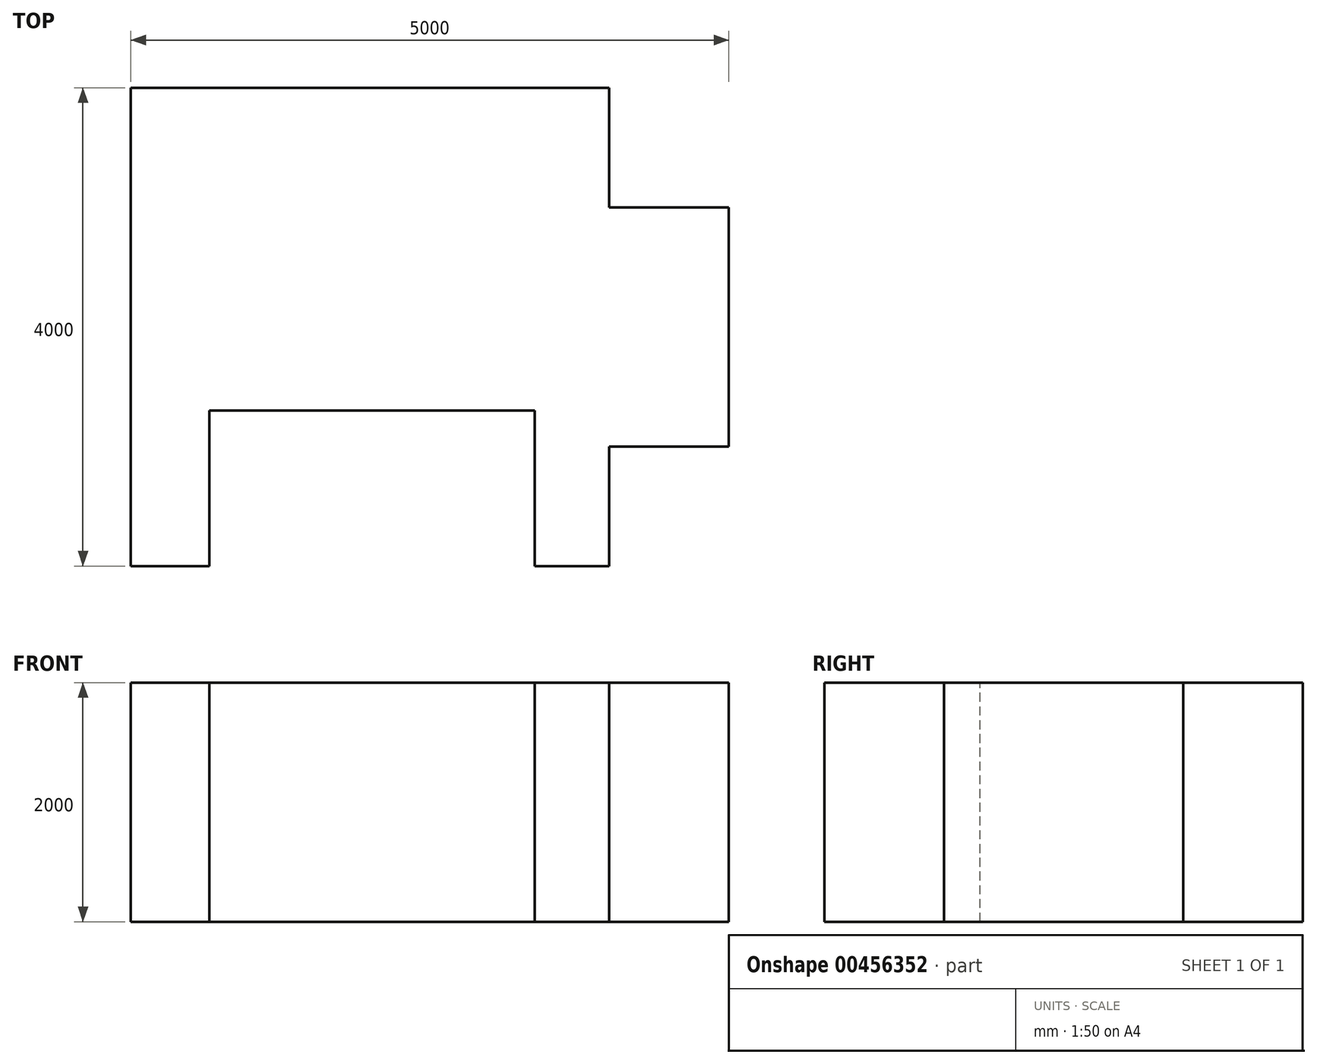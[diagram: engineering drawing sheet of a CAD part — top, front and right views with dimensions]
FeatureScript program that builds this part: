
annotation { "Feature Type Name" : "Feature", "Feature Type Description" : "" }
export const myFeature = defineFeature(function(context is Context, id is Id, definition is map)
    precondition{}
    {
        {
            var Q0;
            Q0=qCreatedBy(makeId("Top.planeOp"),FACE);
            var sketch = newSketch(context, id + "F0", { "sketchPlane" : qUnion([Q0])});
            skLineSegment(sketch, "E0.bottom", {"start": v(0, 0) * mm, "end": v(4000, 0) * mm});
            skLineSegment(sketch, "E0.top", {"start": v(0, 4000) * mm, "end": v(4000, 4000) * mm});
            skLineSegment(sketch, "E0.left", {"start": v(0, 0) * mm, "end": v(0, 4000) * mm});
            skLineSegment(sketch, "E0.right", {"start": v(4000, 0) * mm, "end": v(4000, 1000) * mm});
            skLineSegment(sketch, "E1.bottom", {"start": v(4000, 3000) * mm, "end": v(5000, 3000) * mm});
            skLineSegment(sketch, "E1.top", {"start": v(4000, 1000) * mm, "end": v(5000, 1000) * mm});
            skLineSegment(sketch, "E1.right", {"start": v(5000, 3000) * mm, "end": v(5000, 1000) * mm});
            skLineSegment(sketch, "E2.trimOffspring", {"start": v(4000, 3000) * mm, "end": v(4000, 4000) * mm});
            skSolve(sketch);
        }
        {
            var Q0;
            Q0=makeQuery(id+"F0.imprint","IMPRINT",FACE,{"disambiguationData":[TD([[makeQuery(id+"F0.imprint","IMPRINT",EDGE,{"derivedFrom":sQuery(id+"F0.wireOp",EDGE,"E0.bottom")}),1.0]])]});
            extrude(context, id + "F1", {"entities" : qUnion([Q0]), "depth" : 2000 * mm, "offsetDistance" : 25 * mm});
        }
        {
            var Q0;
            Q0=makeQuery(id+"F1.opExtrude","CAP_FACE",FACE,{"disambiguationData":[OSD([sQuery(id+"F0.wireOp",EDGE,"E0.bottom"),sQuery(id+"F0.wireOp",EDGE,"E0.top"),sQuery(id+"F0.wireOp",EDGE,"E0.left"),sQuery(id+"F0.wireOp",EDGE,"E0.right"),sQuery(id+"F0.wireOp",EDGE,"E1.bottom"),sQuery(id+"F0.wireOp",EDGE,"E1.top"),sQuery(id+"F0.wireOp",EDGE,"E1.right"),sQuery(id+"F0.wireOp",EDGE,"E2.trimOffspring")])],"isStart":false});
            var sketch = newSketch(context, id + "F2", { "sketchPlane" : qUnion([Q0])});
            skLineSegment(sketch, "E3.bottom", {"start": v(3377.68, 1301.88) * mm, "end": v(656.89, 1301.88) * mm});
            skLineSegment(sketch, "E3.top", {"start": v(3377.68, -1090.34) * mm, "end": v(656.89, -1090.34) * mm});
            skLineSegment(sketch, "E3.left", {"start": v(3377.68, 1301.88) * mm, "end": v(3377.68, -1090.34) * mm});
            skLineSegment(sketch, "E3.right", {"start": v(656.89, 1301.88) * mm, "end": v(656.89, -1090.34) * mm});
            skPoint(sketch, "E3.middle", {"position": v(2017.28, 105.77) * mm});
            skSolve(sketch);
        }
        {
            var Q0;
            Q0 = qSketchRegion(id + "F2", true);
            extrude(context, id + "F3", {"entities" : qUnion([Q0]), "operationType" : NewBodyOperationType.REMOVE, "oppositeDirection" : true, "depth" : 2770.14 * mm, "offsetDistance" : 25 * mm});
        }
    });
